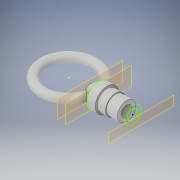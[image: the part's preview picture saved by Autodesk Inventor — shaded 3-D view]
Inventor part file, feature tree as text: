
AUTODESK INVENTOR PART (.ipt)
format: ipt  version: 2018 (Build 220112000, 112)  size: 321,024 bytes
history: native  units: in
note: dims shown in document units (in); Inventor stores cm internally (conversion verified against a paired STEP export)
features: sketch x11, extrude x6, plane x3, revolve x1, loft x1, other x1
ambient origin geometry x8: Origin, YZ Plane, XZ Plane, XY Plane, X Axis, Y Axis, Z Axis, Center Point
bodies: Solid1 (feature_tree)
feature tree (23):
  revolve  "Revolution1"  Angle=90.0deg
  plane  "Work Plane1"
  sketch  "Sketch2"  dims[d2=0.8504in d3=0.1181in]
  plane  "Work Plane2"
  sketch  "Sketch3"  dims[d4=0.1969in d5=0.3504in]
  extrude  "Extrusion1"  Depth=0.8504in
  extrude  "Extrusion2"  Depth=0.3504in
  sketch  "Sketch5"  dims[d6=0.1in d7=0.0in d8=0.1in d9=0.0in]
  sketch  "Sketch6"  dims[d10=0.1in d11=0.0in d12=0.22in d13=0.0in]
  sketch  "Sketch7"  dims[d14=-0.1in d15=0.0in d16=90.0deg]
  extrude  "Extrusion3"  Depth=0.1in TaperAngle=0.0deg
  extrude  "Extrusion4"  Depth=0.1in TaperAngle=0.0deg
  sketch  "Sketch9"  dims[d21=0.17in d22=0.0in]
  plane  "Work Plane3"
  loft  "Loft1"
  extrude  "Extrusion5"  Depth=0.5in TaperAngle=0.0deg
  extrude  "Extrusion6"  [1 undecoded]
  sketch  "Sketch1"  dims[d0=0.0984in d1=90.0deg]
  sketch  "Sketch8"  dims[d17=0.0in d18=90.0deg d19=0.5in d20=0.0in]
  sketch  "Sketch10"
  other  "Edges1"
  sketch  "Sketch11"
  sketch  "Sketch12"
note: 1 required parameter value undecoded (feature->parameter linkage not recoverable at this tier; creation-order binding heuristic only, values carry confidence <= 0.55)
